# Revit family: Furniture-Table-Midmark-627-Power_Examination1
name_source: partatom
category: Furniture
revit_build: Autodesk Revit 2016 (Build: 20170117_1200(x64)
units: mm (PartAtom-declared; Revit-internal decimal feet)

## family parameters
Always vertical = Yes
Cut with Voids When Loaded = No
OmniClass Number = 23.40.70.11.14.11.14
OmniClass Title = Examination and Treatment Equipment
Room Calculation Point = No
Shared = No
Work Plane-Based = No

## types (1)
- 627
    Amps = 12 A
    Apparent Load = 1323 VA
    Assembly Code = E1020810
    Connector Description = Power Connector
    Description = Midmark 627 Barrier-Free Power Examination Table
    Location = This product is meant for the international market.  Not meant for sale in the US.
    Manufacturer = Midmark
    Model = Midmark 627
    Number of Poles = 1
    Patient Weight Capacity = 500.00 lb
    Power Factor = 1
    Product Documentation Link = http://www.midmark.com
    Product Page URL = http://www.midmark.com
    URL = http://www.midmark.com
    Voltage = 115 V
    Weight = 409.00 lb

## geometry (parser evidence)
native form markers: Blend x8, Sweep x30
no freeform markers — native parametric forms only
